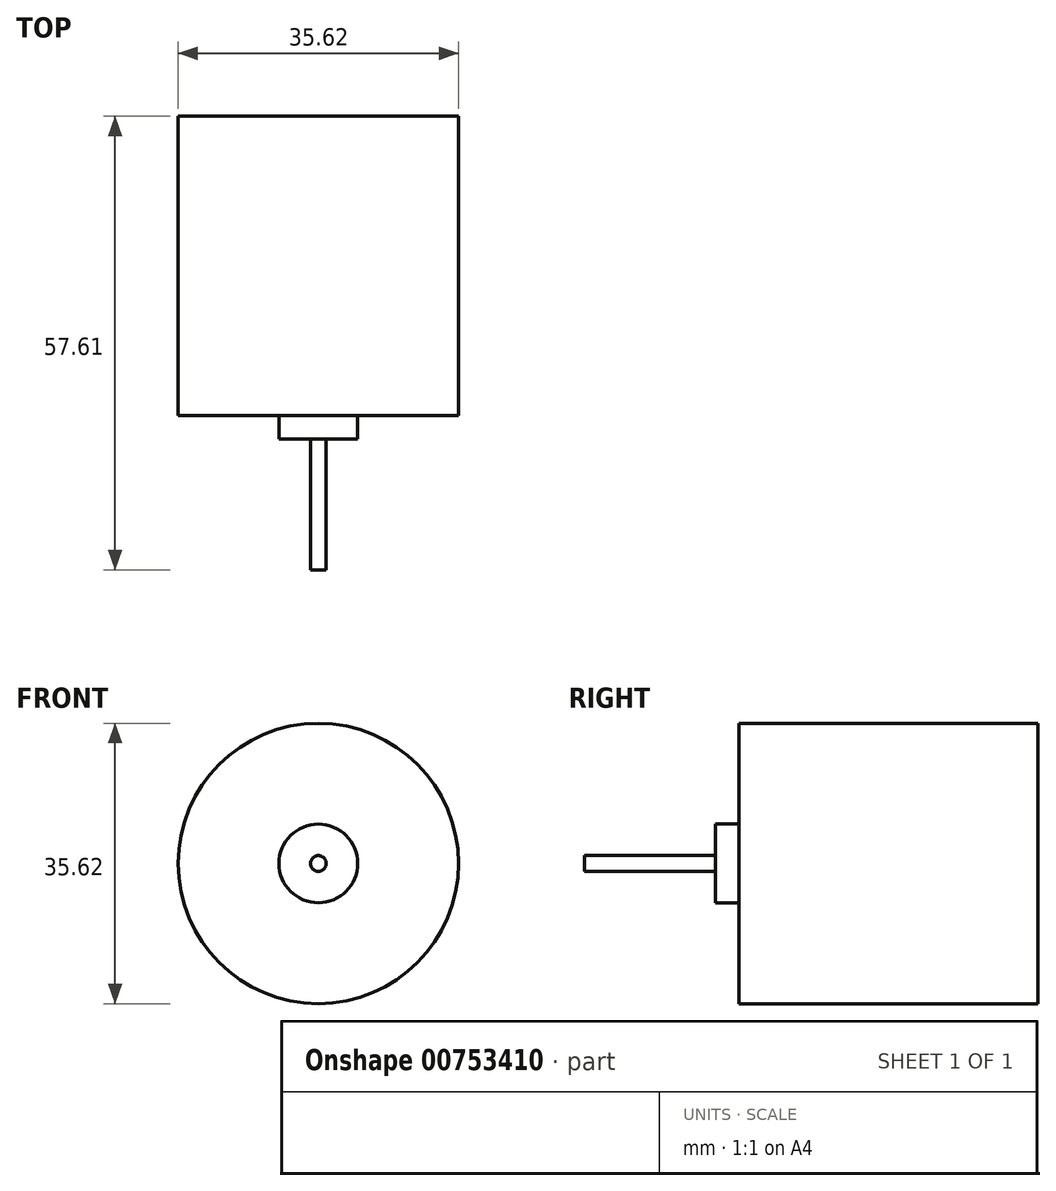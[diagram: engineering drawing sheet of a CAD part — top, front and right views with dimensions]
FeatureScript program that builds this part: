
annotation { "Feature Type Name" : "Feature", "Feature Type Description" : "" }
export const myFeature = defineFeature(function(context is Context, id is Id, definition is map)
    precondition{}
    {
        {
            var Q0;
            Q0=qCreatedBy(makeId("Front.planeOp"),FACE);
            var sketch = newSketch(context, id + "F0", { "sketchPlane" : qUnion([Q0])});
            skCircle(sketch, "E0", {"center": v(0, 0) * mm, "radius": 17.8 * mm});
            skSolve(sketch);
        }
        {
            var Q0;
            Q0 = qSketchRegion(id + "F0", true);
            extrude(context, id + "F1", {"entities" : qUnion([Q0]), "depth" : 38 * mm, "offsetDistance" : 25 * mm, "symmetric" : true});
        }
        {
            var Q0;
            Q0=makeQuery(id+"F1.opExtrude","CAP_FACE",FACE,{"disambiguationData":[OSD([sQuery(id+"F0.wireOp",EDGE,"E0")])],"isStart":false});
            var sketch = newSketch(context, id + "F2", { "sketchPlane" : qUnion([Q0])});
            skCircle(sketch, "E1", {"center": v(0, 0) * mm, "radius": 5 * mm});
            skSolve(sketch);
        }
        {
            var Q0;
            Q0 = qSketchRegion(id + "F2", true);
            extrude(context, id + "F3", {"entities" : qUnion([Q0]), "operationType" : NewBodyOperationType.ADD, "depth" : 3 * mm, "offsetDistance" : 25 * mm});
        }
        {
            var Q0;
            Q0=makeQuery(id+"F3.opExtrude","CAP_FACE",FACE,{"disambiguationData":[OSD([sQuery(id+"F2.wireOp",EDGE,"E1")])],"isStart":false});
            var sketch = newSketch(context, id + "F4", { "sketchPlane" : qUnion([Q0])});
            skCircle(sketch, "E2", {"center": v(0, 0) * mm, "radius": 1 * mm});
            skSolve(sketch);
        }
        {
            var Q0;
            Q0 = qSketchRegion(id + "F4", true);
            extrude(context, id + "F5", {"entities" : qUnion([Q0]), "operationType" : NewBodyOperationType.ADD, "depth" : 16.6 * mm, "offsetDistance" : 25 * mm});
        }
        {
            var Q0;
            Q0=qCreatedBy(makeId("Right.planeOp"),FACE);
            cPlane(context, id + "F6", {"entities" : qUnion([Q0]), "cplaneType" : CPlaneType.OFFSET, "offset" : 18.1 * mm, "width" : 150 * mm, "height" : 150 * mm});
        }
        {
            var Q0;
            Q0=qCreatedBy(id+"F6.planeOp",FACE);
            var sketch = newSketch(context, id + "F7", { "sketchPlane" : qUnion([Q0])});
            skPoint(sketch, "E3", {"position": v(0, 0) * mm});
            skSolve(sketch);
        }
    });
